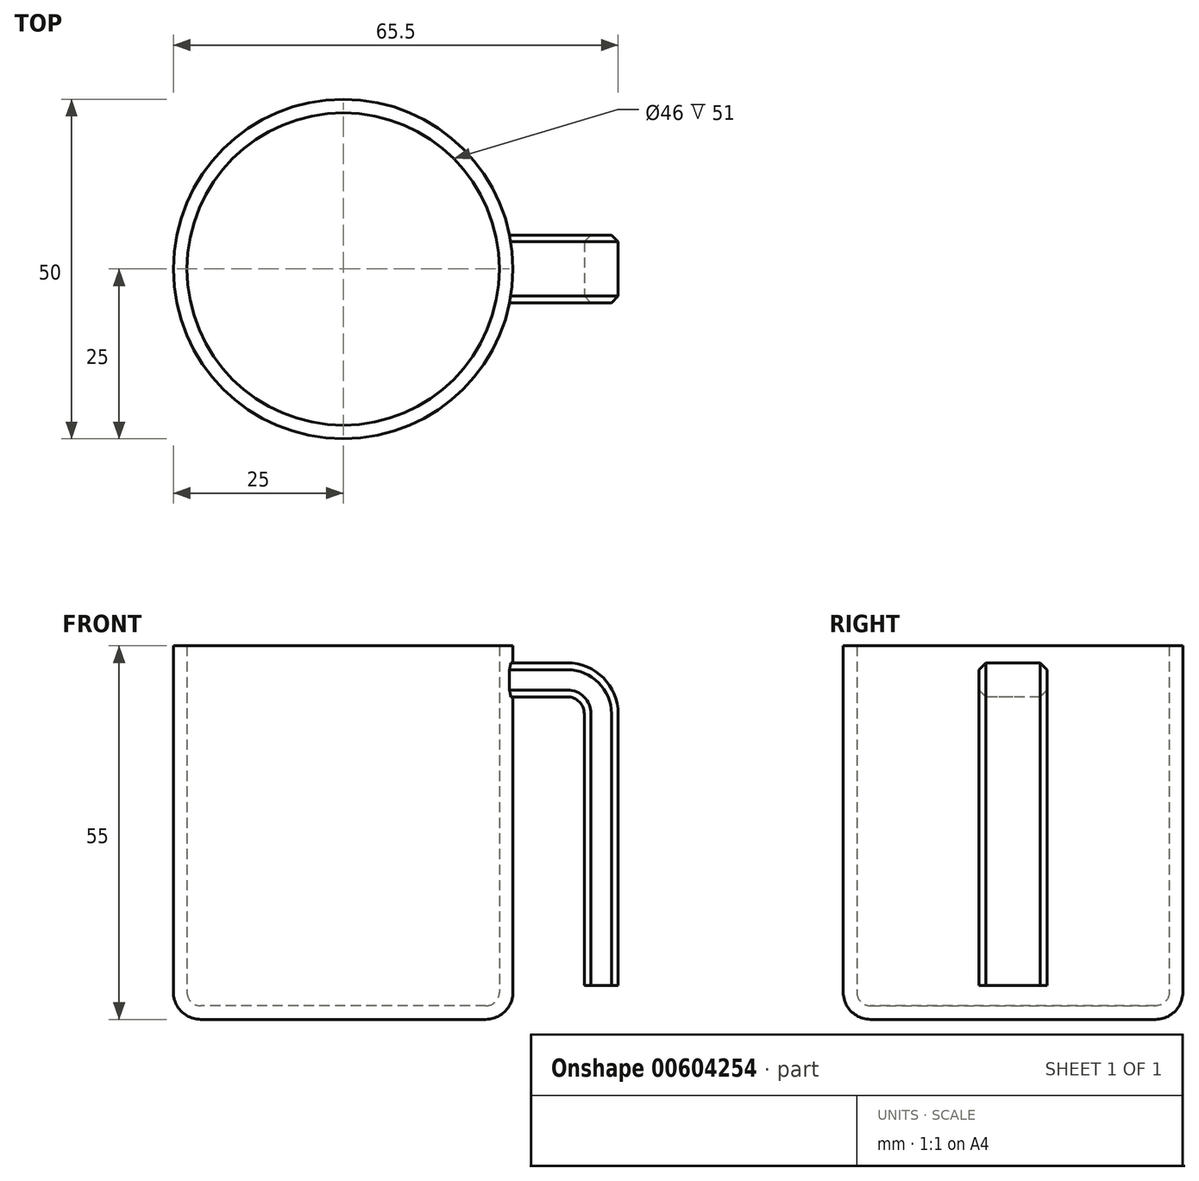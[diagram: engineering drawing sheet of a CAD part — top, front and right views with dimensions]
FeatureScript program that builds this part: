
annotation { "Feature Type Name" : "Feature", "Feature Type Description" : "" }
export const myFeature = defineFeature(function(context is Context, id is Id, definition is map)
    precondition{}
    {
        {
            var Q0;
            Q0=qCreatedBy(makeId("Top.planeOp"),FACE);
            var sketch = newSketch(context, id + "F0", { "sketchPlane" : qUnion([Q0])});
            skCircle(sketch, "E0", {"center": v(0, 0) * mm, "radius": 25 * mm});
            skSolve(sketch);
        }
        {
            var Q0;
            Q0 = qSketchRegion(id + "F0", true);
            extrude(context, id + "F1", {"entities" : qUnion([Q0]), "depth" : 55 * mm, "offsetDistance" : 25 * mm});
        }
        {
            var Q0;
            Q0=makeQuery(id+"F1.opExtrude","CAP_EDGE",EDGE,{"disambiguationData":[OSD([sQuery(id+"F0.wireOp",EDGE,"E0")])],"isStart":true});
            fillet(context, id + "F2", {"entities" : qUnion([Q0]), "radius" : 4 * mm, "tangentPropagation" : true, "allowEdgeOverflow" : false});
        }
        {
            var Q0;
            Q0=makeQuery(id+"F1.opExtrude","CAP_FACE",FACE,{"disambiguationData":[OSD([sQuery(id+"F0.wireOp",EDGE,"E0")])],"isStart":false});
            shell(context, id + "F3", {"entities" : qUnion([Q0]), "thickness" : 2 * mm});
        }
        {
            var Q0;
            Q0=qCreatedBy(makeId("Right.planeOp"),FACE);
            var sketch = newSketch(context, id + "F4", { "sketchPlane" : qUnion([Q0])});
            skLineSegment(sketch, "E1.bottom", {"start": v(5, 52.5) * mm, "end": v(-5, 52.5) * mm});
            skLineSegment(sketch, "E1.top", {"start": v(5, 47.5) * mm, "end": v(-5, 47.5) * mm});
            skLineSegment(sketch, "E1.left", {"start": v(5, 52.5) * mm, "end": v(5, 47.5) * mm});
            skLineSegment(sketch, "E1.right", {"start": v(-5, 52.5) * mm, "end": v(-5, 47.5) * mm});
            skPoint(sketch, "E1.middle", {"position": v(0, 50) * mm});
            skSolve(sketch);
        }
        {
            var Q0;
            Q0=qCreatedBy(makeId("Front.planeOp"),FACE);
            var sketch = newSketch(context, id + "F5", { "sketchPlane" : qUnion([Q0])});
            skLineSegment(sketch, "E2", {"start": v(0, 50) * mm, "end": v(33, 50) * mm});
            skLineSegment(sketch, "E3", {"start": v(38, 45) * mm, "end": v(38, 5) * mm});
            skPoint(sketch, "E4.visualSharp", {"position": v(38, 50) * mm});
            skArc(sketch, "E4.filletArc", {"start": v(38, 45) * mm, "mid": v(36.54, 48.54) * mm, "end": v(33, 50) * mm});
            skSolve(sketch);
        }
        {
            var Q0;
            Q0=makeQuery(id+"F4.imprint","IMPRINT",FACE,{"disambiguationData":[TD([[makeQuery(id+"F4.imprint","IMPRINT",EDGE,{"derivedFrom":sQuery(id+"F4.wireOp",EDGE,"E1.bottom")}),1.0]])]});
            var Q1;
            Q1=sQuery(id+"F5.wireOp",EDGE,"E2");
            var Q2;
            Q2=sQuery(id+"F5.wireOp",EDGE,"E4.filletArc");
            var Q3;
            Q3=sQuery(id+"F5.wireOp",EDGE,"E3");
            sweep(context, id + "F6", {"operationType" : NewBodyOperationType.ADD, "profiles" : qUnion([Q0]), "path" : qUnion([Q1, Q2, Q3])});
        }
        {
            var Q0;
            Q0=makeQuery(id+"F6.opSweep","CAP_FACE",FACE,{"disambiguationData":[OSD([sQuery(id+"F4.wireOp",EDGE,"E1.bottom"),sQuery(id+"F4.wireOp",EDGE,"E1.top"),sQuery(id+"F4.wireOp",EDGE,"E1.left"),sQuery(id+"F4.wireOp",EDGE,"E1.right"),sQuery(id+"F5.wireOp",VERTEX,"E2.start")])],"isStart":true});
            var Q1;
            {var subQ0=sQuery(id+"F0.wireOp",EDGE,"E0");Q1=makeQuery(id+"F3.opShell","OFFSET_FACE",FACE,{"disambiguationData":[OSD([subQ0]),TDD([makeQuery(id+"F1.opExtrude","SWEPT_FACE",FACE,{"disambiguationData":[OSD([subQ0])]})])]});}
            extrude(context, id + "F7", {"entities" : qUnion([Q0]), "operationType" : NewBodyOperationType.REMOVE, "endBound" : BoundingType.UP_TO_SURFACE, "oppositeDirection" : true, "depth" : 25 * mm, "endBoundEntityFace" : qUnion([Q1]), "offsetDistance" : 25 * mm});
        }
        {
            var Q0;
            Q0=makeQuery(id+"F6.opSweep","SWEPT_EDGE",EDGE,{"disambiguationData":[OSD([sQuery(id+"F4.wireOp",EDGE,"E1.bottom"),sQuery(id+"F4.wireOp",EDGE,"E1.left"),sQuery(id+"F5.wireOp",EDGE,"E3")])]});
            var Q1;
            Q1=makeQuery(id+"F6.opSweep","SWEPT_EDGE",EDGE,{"disambiguationData":[OSD([sQuery(id+"F4.wireOp",EDGE,"E1.bottom"),sQuery(id+"F4.wireOp",EDGE,"E1.left"),sQuery(id+"F5.wireOp",EDGE,"E4.filletArc")])]});
            var Q2;
            Q2=makeQuery(id+"F6.opSweep","SWEPT_EDGE",EDGE,{"disambiguationData":[OSD([sQuery(id+"F4.wireOp",EDGE,"E1.bottom"),sQuery(id+"F4.wireOp",EDGE,"E1.right"),sQuery(id+"F5.wireOp",EDGE,"E4.filletArc")])]});
            var Q3;
            Q3=makeQuery(id+"F6.opSweep","SWEPT_EDGE",EDGE,{"disambiguationData":[OSD([sQuery(id+"F4.wireOp",EDGE,"E1.top"),sQuery(id+"F4.wireOp",EDGE,"E1.right"),sQuery(id+"F5.wireOp",EDGE,"E3")])]});
            var Q4;
            Q4=makeQuery(id+"F6.opSweep","SWEPT_EDGE",EDGE,{"disambiguationData":[OSD([sQuery(id+"F4.wireOp",EDGE,"E1.top"),sQuery(id+"F4.wireOp",EDGE,"E1.left"),sQuery(id+"F5.wireOp",EDGE,"E3")])]});
            chamfer(context, id + "F8", {"entities" : qUnion([Q0, Q1, Q2, Q3, Q4]), "width" : 1 * mm, "tangentPropagation" : true});
        }
    });
